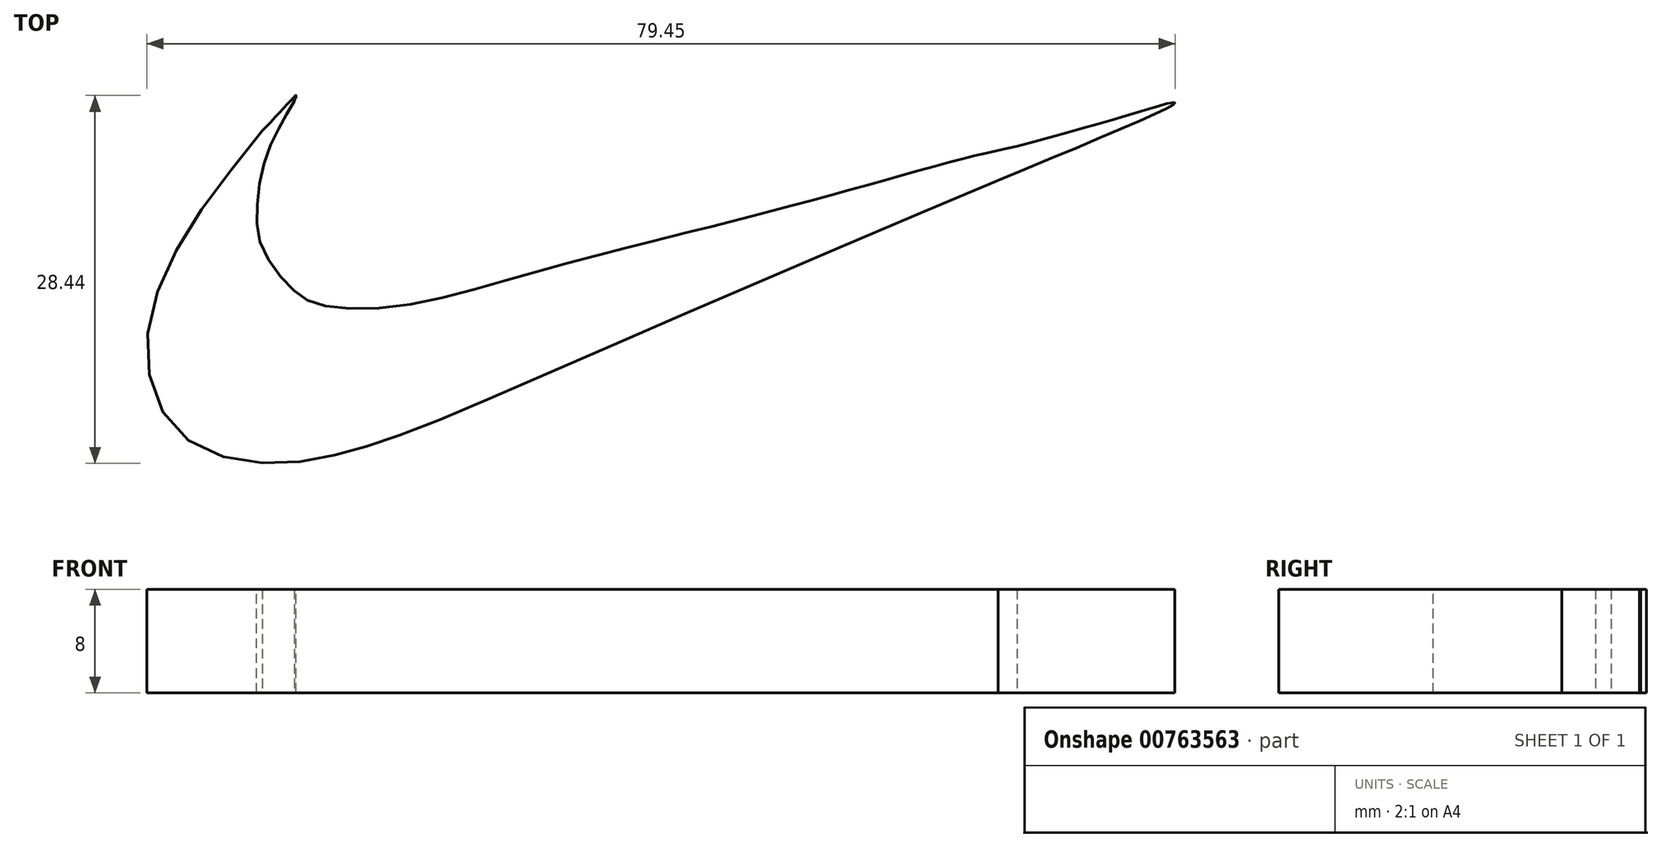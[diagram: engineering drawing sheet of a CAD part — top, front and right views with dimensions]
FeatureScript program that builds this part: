
annotation { "Feature Type Name" : "Feature", "Feature Type Description" : "" }
export const myFeature = defineFeature(function(context is Context, id is Id, definition is map)
    precondition{}
    {
        {
            var Q0;
            Q0=qCreatedBy(makeId("Top.planeOp"),FACE);
            var sketch = newSketch(context, id + "F0", { "sketchPlane" : qUnion([Q0])});
            skFitSpline(sketch, "E0", {"points": [v(-31.93, 42.1) * mm, v(-32.98, 40.27) * mm, v(-34.23, 37.38) * mm, v(-34.81, 33.7) * mm, v(-34.4, 30.74) * mm, v(-32.21, 27.7) * mm, v(-30.09, 26.4) * mm, v(-23.66, 26.29) * mm, v(-14.64, 28.52) * mm, v(-6.22, 30.77) * mm], "startDerivative": vector(-13.34, -22.64) * mm, "endDerivative": vector(53.4, 13.78) * mm});
            skFitSpline(sketch, "E1", {"points": [v(-6.22, 30.77) * mm, v(9.2, 34.75) * mm, v(19.4, 37.57) * mm, v(23.94, 38.61) * mm], "startDerivative": vector(37.5, 9.4) * mm, "endDerivative": vector(18, 3.82) * mm});
            skFitSpline(sketch, "E2", {"points": [v(23.94, 38.61) * mm, v(33.08, 41.2) * mm, v(35.97, 42) * mm, v(36.14, 41.96) * mm, v(22.46, 36) * mm], "startDerivative": vector(29.7, 8.2) * mm, "endDerivative": vector(-48.04, -19.82) * mm});
            skFitSpline(sketch, "E3", {"points": [v(22.46, 36) * mm, v(-7.24, 23.28) * mm, v(-22.71, 16.67) * mm, v(-28.08, 14.92) * mm, v(-33.94, 14.11) * mm, v(-40.5, 16.17) * mm, v(-43.3, 22.4) * mm, v(-40.93, 30.77) * mm, v(-34.38, 39.81) * mm], "startDerivative": vector(-144.2, -61.26) * mm, "endDerivative": vector(56.65, 69.51) * mm});
            skFitSpline(sketch, "E4", {"points": [v(-34.38, 39.81) * mm, v(-32.08, 42.29) * mm, v(-31.78, 42.55) * mm, v(-31.93, 42.1) * mm], "startDerivative": vector(4.7, 5.05) * mm, "endDerivative": vector(-1.14, -2.86) * mm});
            skSolve(sketch);
        }
        {
            var Q0;
            Q0 = qSketchRegion(id + "F0", true);
            extrude(context, id + "F1", {"entities" : qUnion([Q0]), "depth" : 8 * mm, "offsetDistance" : 25.4 * mm});
        }
    });
